# Revit family: CDL6
name_source: partatom
category: Lighting Fixtures
revit_build: Autodesk Revit 2014 (Build: 20130308_1515(x64)
units: mm (PartAtom-declared; Revit-internal decimal feet)

## types (1)
- CDL6
    Apparent Load = 11 VA
    Assembly Code = D5020210
    Color Filter = 16777215
    Default Elevation = 22 "
    Description = The CDL4 and CDL6 are recessed downlights designed for new
construction or retrofit applications. Each downlight is offered
in 3000K color temperature, with a CRI of 90 for exceptional
color rendering. The dimming range is from 100 - 10%. The CDL
series is designed to meet Energy Star and California Title 24
standards for residential and non-residential applications.
    Dimming Lamp Color Temperature Shift = <None>
    Emit Shape Visible in Rendering = No
    Emit from Circle Diameter = 3 "
    Housing Material = Paint - Hubbell - Matte White
    Inner Dia = 3.625 "
    Lamp = LED
    Load Classification = Lighting
    Manufacturer = Prescolite
    Model = CDL6
    Outter Dia = 7.5 "
    Photometric Notes = More IES files download on Photometric Web Link
    Photometric Web File = CDL6_8L30KAWH.ies
    Photometric Web Link = https://www.hubbell.com
    Power Factor = 0.9
    Product Documentation Link = https://hubbellcdn.com
    Product Name = CDL6
    Product Page URL = https://www.hubbell.com
    Tilt Angle = -90.00°
    Type Comments = Lighting Fixture
    URL = https://www.hubbell.com
    Voltage = 120 V
    Warranty = 5 Year Warranty
    Watts = 10 W

## geometry (parser evidence)
native form markers: Blend x8, Sweep x1
no freeform markers — native parametric forms only
